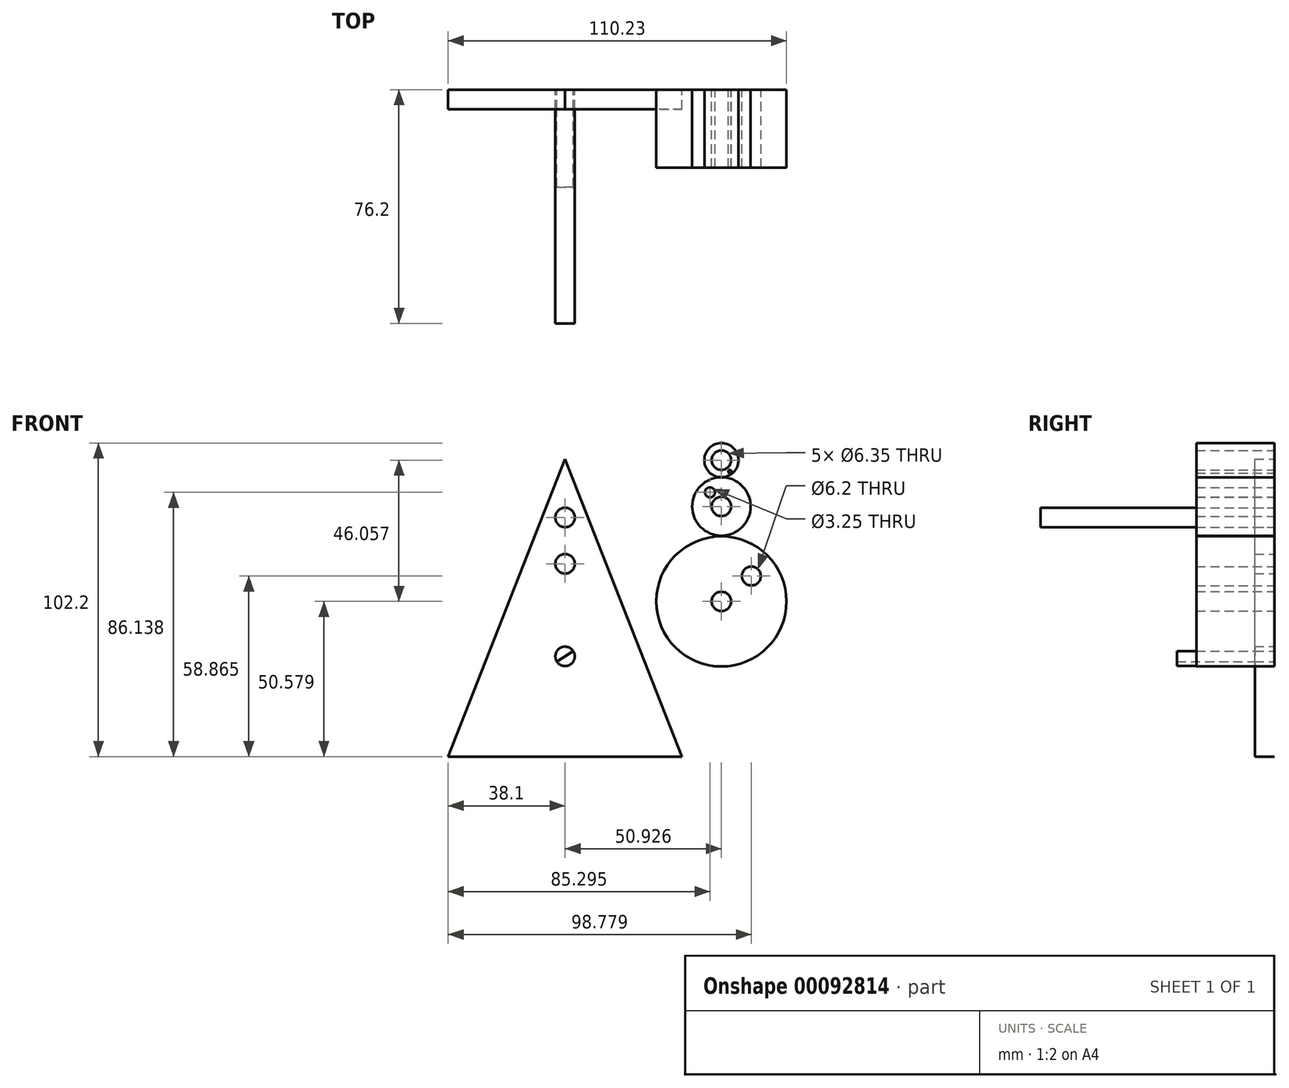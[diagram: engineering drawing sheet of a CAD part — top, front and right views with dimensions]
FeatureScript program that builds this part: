
annotation { "Feature Type Name" : "Feature", "Feature Type Description" : "" }
export const myFeature = defineFeature(function(context is Context, id is Id, definition is map)
    precondition{}
    {
        {
            var Q0;
            Q0=qCreatedBy(makeId("Front.planeOp"),FACE);
            var sketch = newSketch(context, id + "F0", { "sketchPlane" : qUnion([Q0])});
            skCircle(sketch, "E0", {"center": v(0, 0) * mm, "radius": 18.25 * mm});
            skLineSegment(sketch, "E1", {"start": v(0, 0) * mm, "end": v(0, 30.18) * mm});
            skCircle(sketch, "E2", {"center": v(0, 30.18) * mm, "radius": 8.73 * mm});
            skLineSegment(sketch, "E3", {"start": v(0, 30.18) * mm, "end": v(0, 45.26) * mm});
            skCircle(sketch, "E4", {"center": v(0, 45.26) * mm, "radius": 3.97 * mm});
            skPoint(sketch, "E5.middle", {"position": v(0, 21.44) * mm});
            skLineSegment(sketch, "E6.left", {"start": v(0, 0) * mm, "end": v(0, 30.48) * mm});
            skLineSegment(sketch, "E7.left", {"start": v(0, 18.25) * mm, "end": v(0, 21.44) * mm});
            skPoint(sketch, "E8.end.orphan", {"position": v(0, -32.68) * mm});
            skLineSegment(sketch, "E9.trimOffspring", {"start": v(0, 30.18) * mm, "end": v(0, 30.48) * mm});
            skLineSegment(sketch, "E10", {"start": v(-38.1, -32.68) * mm, "end": v(38.1, -32.68) * mm});
            skLineSegment(sketch, "E11", {"start": v(0, 45.26) * mm, "end": v(0, 64.31) * mm});
            skLineSegment(sketch, "E12", {"start": v(-38.1, -32.68) * mm, "end": v(0, 64.31) * mm});
            skLineSegment(sketch, "E13", {"start": v(38.1, -32.68) * mm, "end": v(0, 64.31) * mm});
            skCircle(sketch, "E14", {"center": v(0, 0) * mm, "radius": 3.18 * mm});
            skLineSegment(sketch, "E15", {"start": v(2.66, 1.73) * mm, "end": v(-2.7, -1.67) * mm});
            skCircle(sketch, "E16", {"center": v(0, 30.18) * mm, "radius": 3.18 * mm});
            skCircle(sketch, "E17", {"center": v(0, 45.26) * mm, "radius": 3.18 * mm});
            skSolve(sketch);
        }
        {
            var Q0;
            Q0=makeQuery(id+"F0.imprint","IMPRINT",FACE,{"disambiguationData":[TD([[makeQuery(id+"F0.imprint","IMPRINT",EDGE,{"derivedFrom":sQuery(id+"F0.wireOp",EDGE,"E0")}),-1.0]])]});
            var Q1;
            Q1=makeQuery(id+"F0.imprint","IMPRINT",FACE,{"disambiguationData":[TD([[makeQuery(id+"F0.imprint","IMPRINT",EDGE,{"derivedFrom":sQuery(id+"F0.wireOp",EDGE,"E0")}),1.0]])]});
            var Q2;
            {var subQ0=sQuery(id+"F0.wireOp",EDGE,"E6.left");var subQ1=sQuery(id+"F0.wireOp",EDGE,"E2");var subQ2=makeQuery(id+"F0.imprint","INTERSECT",VERTEX,{"derivedFrom":[subQ1,subQ0]});Q2=makeQuery(id+"F0.imprint","IMPRINT",FACE,{"disambiguationData":[TD([[makeQuery(id+"F0.imprint","IMPRINT",EDGE,{"disambiguationData":[TD([[subQ2,1.0]])],"derivedFrom":subQ1}),1.0]])]});}
            var Q3;
            {var subQ0=sQuery(id+"F0.wireOp",EDGE,"E6.left");var subQ1=sQuery(id+"F0.wireOp",EDGE,"E2");var subQ2=makeQuery(id+"F0.imprint","INTERSECT",VERTEX,{"derivedFrom":[subQ1,subQ0]});Q3=makeQuery(id+"F0.imprint","IMPRINT",FACE,{"disambiguationData":[TD([[makeQuery(id+"F0.imprint","IMPRINT",EDGE,{"disambiguationData":[TD([[subQ2,-1.0]])],"derivedFrom":subQ1}),1.0]])]});}
            var Q4;
            {var subQ0=sQuery(id+"F0.wireOp",EDGE,"E4");var subQ1=sQuery(id+"F0.wireOp",EDGE,"E3");var subQ2=makeQuery(id+"F0.imprint","INTERSECT",VERTEX,{"derivedFrom":[subQ1,subQ0]});Q4=makeQuery(id+"F0.imprint","IMPRINT",FACE,{"disambiguationData":[TD([[makeQuery(id+"F0.imprint","IMPRINT",EDGE,{"disambiguationData":[TD([[subQ2,-1.0]])],"derivedFrom":subQ1}),-1.0]])]});}
            var Q5;
            {var subQ0=sQuery(id+"F0.wireOp",EDGE,"E4");var subQ1=sQuery(id+"F0.wireOp",EDGE,"E3");var subQ2=makeQuery(id+"F0.imprint","INTERSECT",VERTEX,{"derivedFrom":[subQ1,subQ0]});Q5=makeQuery(id+"F0.imprint","IMPRINT",FACE,{"disambiguationData":[TD([[makeQuery(id+"F0.imprint","IMPRINT",EDGE,{"disambiguationData":[TD([[subQ2,-1.0]])],"derivedFrom":subQ1}),1.0]])]});}
            extrude(context, id + "F1", {"entities" : qUnion([Q0, Q1, Q2, Q3, Q4, Q5]), "depth" : 6.35 * mm});
        }
        {
            var Q0;
            {var subQ0=sQuery(id+"F0.wireOp",EDGE,"E15");var subQ1=sQuery(id+"F0.wireOp",EDGE,"E14");var subQ2=makeQuery(id+"F0.imprint","INTERSECT",VERTEX,{"disambiguationData":[OD(0.0)],"derivedFrom":[subQ1,subQ0]});Q0=makeQuery(id+"F0.imprint","IMPRINT",FACE,{"disambiguationData":[TD([[makeQuery(id+"F0.imprint","IMPRINT",EDGE,{"disambiguationData":[TD([[subQ2,1.0]])],"derivedFrom":subQ1}),1.0]])]});}
            var Q1;
            {var subQ0=sQuery(id+"F0.wireOp",EDGE,"E14");var subQ1=sQuery(id+"F0.wireOp",EDGE,"E6.left");var subQ2=makeQuery(id+"F0.imprint","INTERSECT",VERTEX,{"derivedFrom":[subQ1,subQ0]});Q1=makeQuery(id+"F0.imprint","IMPRINT",FACE,{"disambiguationData":[TD([[makeQuery(id+"F0.imprint","IMPRINT",EDGE,{"disambiguationData":[TD([[subQ2,1.0]])],"derivedFrom":subQ1}),1.0]])]});}
            var Q2;
            {var subQ0=sQuery(id+"F0.wireOp",EDGE,"E14");var subQ1=sQuery(id+"F0.wireOp",EDGE,"E6.left");var subQ2=makeQuery(id+"F0.imprint","INTERSECT",VERTEX,{"derivedFrom":[subQ1,subQ0]});Q2=makeQuery(id+"F0.imprint","IMPRINT",FACE,{"disambiguationData":[TD([[makeQuery(id+"F0.imprint","IMPRINT",EDGE,{"disambiguationData":[TD([[subQ2,1.0]])],"derivedFrom":subQ1}),-1.0]])]});}
            extrude(context, id + "F2", {"entities" : qUnion([Q0, Q1, Q2]), "operationType" : NewBodyOperationType.ADD, "depth" : 31.75 * mm});
        }
        {
            var Q0;
            {var subQ0=sQuery(id+"F0.wireOp",EDGE,"E9.trimOffspring");Q0=makeQuery(id+"F0.imprint","IMPRINT",FACE,{"disambiguationData":[TD([[makeQuery(id+"F0.imprint","IMPRINT",EDGE,{"derivedFrom":subQ0}),1.0]])]});}
            var Q1;
            {var subQ0=sQuery(id+"F0.wireOp",EDGE,"E9.trimOffspring");Q1=makeQuery(id+"F0.imprint","IMPRINT",FACE,{"disambiguationData":[TD([[makeQuery(id+"F0.imprint","IMPRINT",EDGE,{"derivedFrom":subQ0}),-1.0]])]});}
            var Q2;
            {var subQ0=sQuery(id+"F0.wireOp",EDGE,"E11");var subQ1=sQuery(id+"F0.wireOp",EDGE,"E3");var subQ2=makeQuery(id+"F0.imprint","INTERSECT",VERTEX,{"derivedFrom":[subQ1,subQ0]});Q2=makeQuery(id+"F0.imprint","IMPRINT",FACE,{"disambiguationData":[TD([[makeQuery(id+"F0.imprint","IMPRINT",EDGE,{"disambiguationData":[TD([[subQ2,1.0]])],"derivedFrom":subQ1}),-1.0]])]});}
            var Q3;
            {var subQ0=sQuery(id+"F0.wireOp",EDGE,"E11");var subQ1=sQuery(id+"F0.wireOp",EDGE,"E3");var subQ2=makeQuery(id+"F0.imprint","INTERSECT",VERTEX,{"derivedFrom":[subQ1,subQ0]});Q3=makeQuery(id+"F0.imprint","IMPRINT",FACE,{"disambiguationData":[TD([[makeQuery(id+"F0.imprint","IMPRINT",EDGE,{"disambiguationData":[TD([[subQ2,1.0]])],"derivedFrom":subQ1}),1.0]])]});}
            extrude(context, id + "F3", {"entities" : qUnion([Q0, Q1, Q2, Q3]), "depth" : 76.2 * mm});
        }
        {
            var Q0;
            Q0=makeQuery(id+"F0.imprint","IMPRINT",FACE,{"disambiguationData":[TD([[makeQuery(id+"F0.imprint","IMPRINT",EDGE,{"derivedFrom":sQuery(id+"F0.wireOp",EDGE,"E0")}),-1.0]])]});
            var sketch = newSketch(context, id + "F4", { "sketchPlane" : qUnion([Q0])});
            skCircle(sketch, "E18", {"center": v(50.93, 17.9) * mm, "radius": 21.2 * mm});
            skLineSegment(sketch, "E19", {"start": v(50.93, 17.9) * mm, "end": v(50.93, 17.94) * mm});
            skCircle(sketch, "E20", {"center": v(50.93, 48.87) * mm, "radius": 9.53 * mm});
            skLineSegment(sketch, "E21", {"start": v(50.93, 48.87) * mm, "end": v(50.93, 49.17) * mm});
            skCircle(sketch, "E22", {"center": v(50.93, 63.96) * mm, "radius": 5.56 * mm});
            skPoint(sketch, "E23.middle", {"position": v(50.93, 39.34) * mm});
            skPoint(sketch, "E24.end.orphan", {"position": v(50.93, -14.78) * mm});
            skLineSegment(sketch, "E25", {"start": v(12.83, -14.78) * mm, "end": v(89.03, -14.78) * mm});
            skLineSegment(sketch, "E26", {"start": v(50.93, 67.13) * mm, "end": v(50.93, 69.52) * mm});
            skCircle(sketch, "E27", {"center": v(50.93, 17.9) * mm, "radius": 3.18 * mm});
            skCircle(sketch, "E28", {"center": v(50.93, 48.87) * mm, "radius": 3.18 * mm});
            skCircle(sketch, "E29", {"center": v(50.93, 63.96) * mm, "radius": 3.18 * mm});
            skLineSegment(sketch, "E30.trimOffspring", {"start": v(50.93, 58.4) * mm, "end": v(50.93, 60.78) * mm});
            skCircle(sketch, "E31", {"center": v(60.68, 26.19) * mm, "radius": 3.1 * mm});
            skCircle(sketch, "E32", {"center": v(47.2, 53.46) * mm, "radius": 1.62 * mm});
            skCircle(sketch, "E33", {"center": v(53.65, 60.25) * mm, "radius": 0.54 * mm});
            skSolve(sketch);
        }
        {
            var Q0;
            Q0=makeQuery(id+"F4.imprint","IMPRINT",FACE,{"disambiguationData":[TD([[makeQuery(id+"F4.imprint","IMPRINT",EDGE,{"derivedFrom":sQuery(id+"F4.wireOp",EDGE,"E18")}),1.0]])]});
            var Q1;
            Q1=makeQuery(id+"F4.imprint","IMPRINT",FACE,{"disambiguationData":[TD([[makeQuery(id+"F4.imprint","IMPRINT",EDGE,{"derivedFrom":sQuery(id+"F4.wireOp",EDGE,"E20")}),1.0]])]});
            var Q2;
            {var subQ0=sQuery(id+"F4.wireOp",EDGE,"E26");Q2=makeQuery(id+"F4.imprint","IMPRINT",FACE,{"disambiguationData":[TD([[makeQuery(id+"F4.imprint","IMPRINT",EDGE,{"derivedFrom":subQ0}),1.0]])]});}
            var Q3;
            {var subQ0=sQuery(id+"F4.wireOp",EDGE,"E26");Q3=makeQuery(id+"F4.imprint","IMPRINT",FACE,{"disambiguationData":[TD([[makeQuery(id+"F4.imprint","IMPRINT",EDGE,{"derivedFrom":subQ0}),-1.0]])]});}
            extrude(context, id + "F5", {"entities" : qUnion([Q0, Q1, Q2, Q3]), "depth" : 25.4 * mm});
        }
        {
            var Q0;
            Q0=makeQuery(id+"F4.imprint","IMPRINT",FACE,{"disambiguationData":[TD([[makeQuery(id+"F4.imprint","IMPRINT",EDGE,{"derivedFrom":sQuery(id+"F4.wireOp",EDGE,"E27")}),-1.0]])]});
            extrude(context, id + "F6", {"entities" : qUnion([Q0]), "operationType" : NewBodyOperationType.ADD, "depth" : 25.4 * mm});
        }
    });
